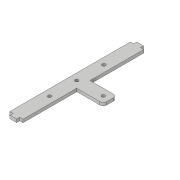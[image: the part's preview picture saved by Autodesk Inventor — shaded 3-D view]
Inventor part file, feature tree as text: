
AUTODESK INVENTOR PART (.ipt)
format: ipt  version: 2017 (Build 210142000, 142)  size: 127,488 bytes
history: native  units: in
note: dims shown in document units (in); Inventor stores cm internally (conversion verified against a paired STEP export)
features: extrude x4, sketch x4
ambient origin geometry x8: Origin, YZ Plane, XZ Plane, XY Plane, X Axis, Y Axis, Z Axis, Center Point
bodies: Solid1 (feature_tree)
feature tree (8):
  extrude  "Extrusion1"  Depth=0.5in
  extrude  "Extrusion2"  Depth=0.125in
  extrude  "Extrusion3"  Depth=0.115in
  extrude  "Extrusion4"  Depth=0.115in TaperAngle=0.0deg
  sketch  "Sketch1"  dims[d0=4.54in d1=0.5in]
  sketch  "Sketch2"  dims[d2=0.25in d3=0.125in]
  sketch  "Sketch3"  dims[d4=0.115in d5=0.115in]
  sketch  "Sketch4"  dims[d6=0.125in d7=0.115in d8=0.0in d9=0.125in d10=0.125in d11=0.25in d12=0.25in d13=1.25in d14=1.25in d15=0.115in d16=0.0in d17=0.125in d18=0.25in d19=2.27in d20=0.115in d21=0.0in d22=0.25in d23=0.5in d24=1.0in d25=0.0in d26=0.125in d27=1.0in d28=0.125in d29=0.11in d30=0.0in]
